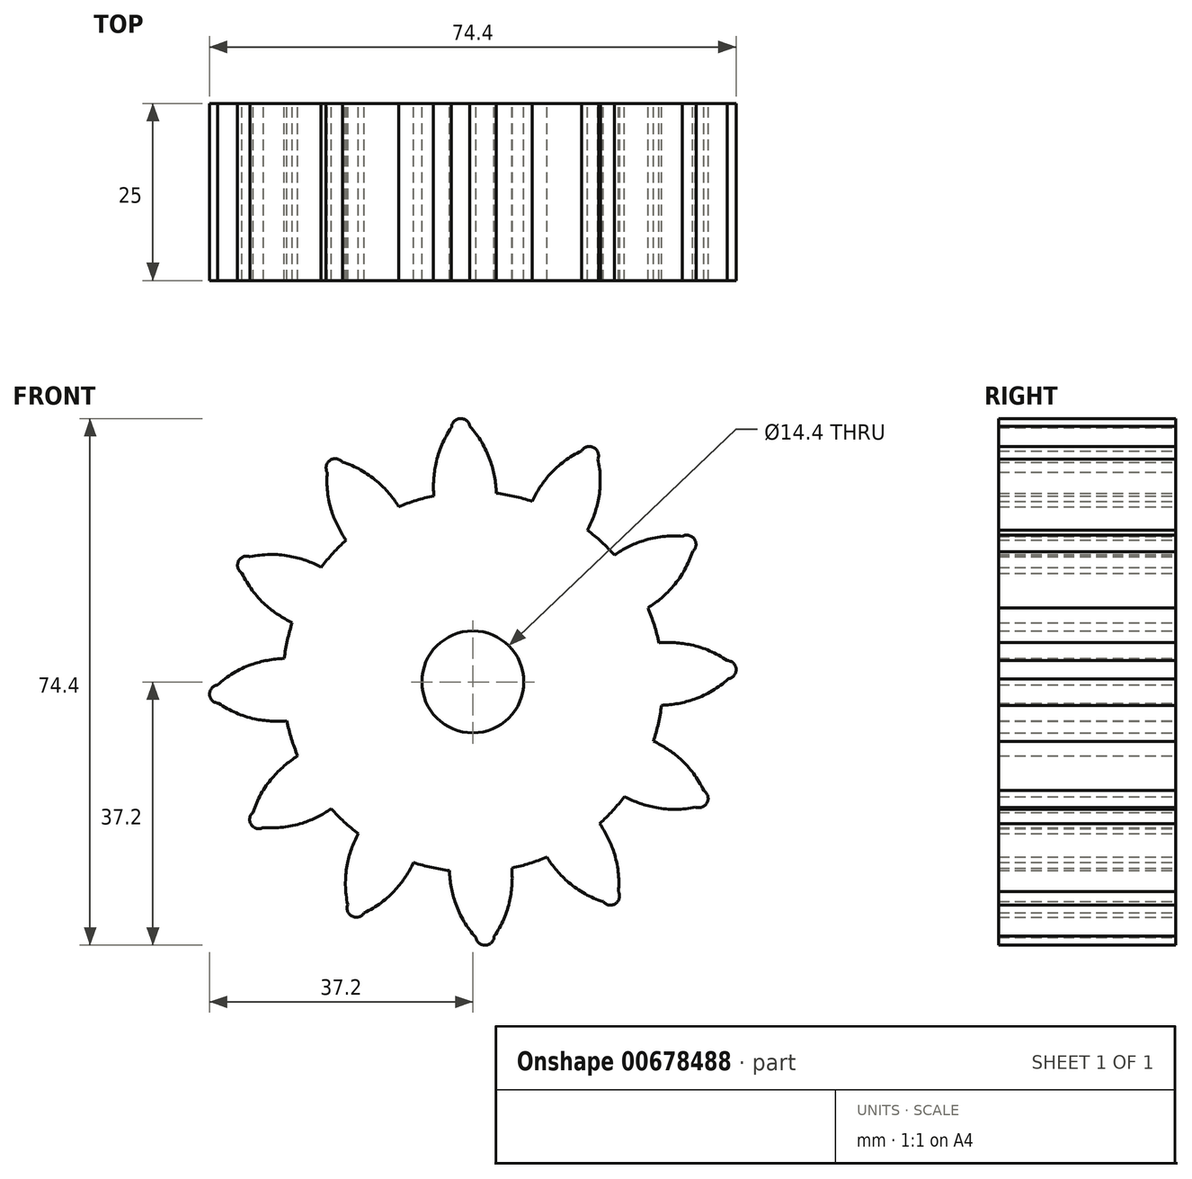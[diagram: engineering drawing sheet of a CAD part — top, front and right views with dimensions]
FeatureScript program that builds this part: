
annotation { "Feature Type Name" : "Feature", "Feature Type Description" : "" }
export const myFeature = defineFeature(function(context is Context, id is Id, definition is map)
    precondition{}
    {
        {
            var Q0;
            Q0=qCreatedBy(makeId("Front.planeOp"),FACE);
            var sketch = newSketch(context, id + "F0", { "sketchPlane" : qUnion([Q0])});
            skCircle(sketch, "E0", {"center": v(0, 0) * mm, "radius": 26.86 * mm});
            skCircle(sketch, "E1", {"center": v(0, 0) * mm, "radius": 29.34 * mm, "construction": true});
            skCircle(sketch, "E2", {"center": v(0, 0) * mm, "radius": 31.75 * mm, "construction": true});
            skCircle(sketch, "E3", {"center": v(-11.3, 26.33) * mm, "radius": 14.6 * mm, "construction": true});
            skArc(sketch, "E4", {"start": v(2.43, 31.33) * mm, "mid": v(1.24, 33.85) * mm, "end": v(-0.42, 36.09) * mm});
            skArc(sketch, "E5", {"start": v(3.31, 26.37) * mm, "mid": v(3.08, 28.88) * mm, "end": v(2.43, 31.33) * mm});
            skArc(sketch, "E6.MirrorCS", {"start": v(-5.23, 30.82) * mm, "mid": v(-4.38, 33.48) * mm, "end": v(-3.02, 35.92) * mm});
            skArc(sketch, "E7.MirrorCS", {"start": v(-5.45, 25.8) * mm, "mid": v(-5.55, 28.32) * mm, "end": v(-5.23, 30.82) * mm});
            skArc(sketch, "E8", {"start": v(-0.42, 36.09) * mm, "mid": v(-1.8, 37.2) * mm, "end": v(-3.02, 35.92) * mm});
            skCircle(sketch, "E9", {"center": v(0, 0) * mm, "radius": 7.2 * mm});
            skSolve(sketch);
        }
        {
            var Q0;
            Q0=makeQuery(id+"F0.imprint","IMPRINT",FACE,{"disambiguationData":[TD([[makeQuery(id+"F0.imprint","IMPRINT",EDGE,{"derivedFrom":sQuery(id+"F0.wireOp",EDGE,"E0")}),1.0]])]});
            var Q1;
            {var subQ2=sQuery(id+"F0.wireOp",EDGE,"E4");Q1=makeQuery(id+"F0.imprint","IMPRINT",FACE,{"disambiguationData":[TD([[makeQuery(id+"F0.imprint","IMPRINT",EDGE,{"derivedFrom":subQ2}),1.0]])]});}
            extrude(context, id + "F1", {"entities" : qUnion([Q0, Q1]), "depth" : 25 * mm, "offsetDistance" : 25 * mm});
        }
        {
            var Q0;
            Q0=makeQuery(id+"F1.opExtrude","SWEPT_BODY",BODY,{"disambiguationData":[OSD([sQuery(id+"F0.wireOp",EDGE,"E0"),sQuery(id+"F0.wireOp",EDGE,"E4"),sQuery(id+"F0.wireOp",EDGE,"E5"),sQuery(id+"F0.wireOp",EDGE,"E6.MirrorCS"),sQuery(id+"F0.wireOp",EDGE,"E7.MirrorCS"),sQuery(id+"F0.wireOp",EDGE,"E8")])]});
            var Q1;
            Q1=makeQuery(id+"F1.opExtrude","SWEPT_FACE",FACE,{"disambiguationData":[OSD([sQuery(id+"F0.wireOp",EDGE,"E0")])]});
            circularPattern(context, id + "F2", {"operationType" : NewBodyOperationType.ADD, "entities" : qUnion([Q0]), "axis" : qUnion([Q1]), "angle" : 360 * degree, "instanceCount" : 12, "equalSpace" : true});
        }
    });
